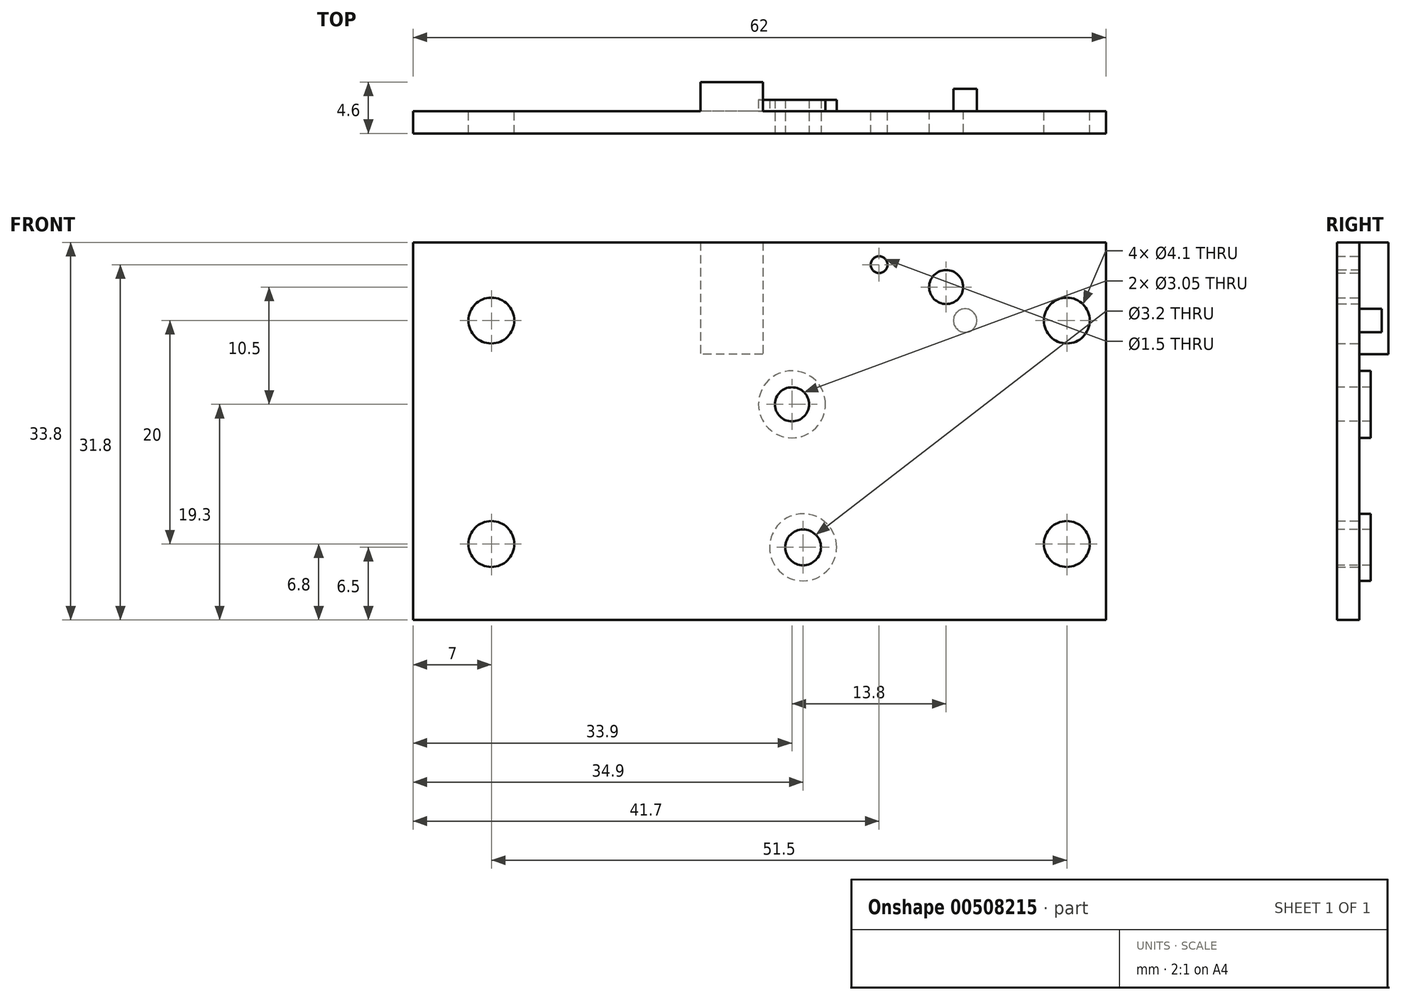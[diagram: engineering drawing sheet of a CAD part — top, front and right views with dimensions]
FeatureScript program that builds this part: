
annotation { "Feature Type Name" : "Feature", "Feature Type Description" : "" }
export const myFeature = defineFeature(function(context is Context, id is Id, definition is map)
    precondition{}
    {
        {
            var Q0;
            Q0=qCreatedBy(makeId("Front.planeOp"),FACE);
            var sketch = newSketch(context, id + "F0", { "sketchPlane" : qUnion([Q0])});
            skLineSegment(sketch, "E0.bottom", {"start": v(31, -16.9) * mm, "end": v(-31, -16.9) * mm});
            skLineSegment(sketch, "E0.top", {"start": v(31, 16.9) * mm, "end": v(-31, 16.9) * mm});
            skLineSegment(sketch, "E0.left", {"start": v(31, -16.9) * mm, "end": v(31, 16.9) * mm});
            skLineSegment(sketch, "E0.right", {"start": v(-31, -16.9) * mm, "end": v(-31, 16.9) * mm});
            skPoint(sketch, "E0.middle", {"position": v(0, 0) * mm});
            skCircle(sketch, "E1", {"center": v(16.7, 12.9) * mm, "radius": 1.52 * mm});
            skCircle(sketch, "E2", {"center": v(2.9, 2.4) * mm, "radius": 1.52 * mm});
            skCircle(sketch, "E3", {"center": v(3.9, -10.4) * mm, "radius": 1.6 * mm});
            skArc(sketch, "E4", {"start": v(6.45, 16.9) * mm, "mid": v(10.88, 3.57) * mm, "end": v(24.8, 5.46) * mm});
            skLineSegment(sketch, "E5", {"start": v(24.8, 16.9) * mm, "end": v(24.8, -16.9) * mm});
            skSolve(sketch);
        }
        {
            var Q0;
            {var subQ0=sQuery(id+"F0.wireOp",EDGE,"E0.right");Q0=makeQuery(id+"F0.imprint","IMPRINT",FACE,{"disambiguationData":[TD([[makeQuery(id+"F0.imprint","IMPRINT",EDGE,{"derivedFrom":subQ0}),-1.0]])]});}
            var Q1;
            Q1=makeQuery(id+"F0.imprint","IMPRINT",FACE,{"disambiguationData":[TD([[makeQuery(id+"F0.imprint","IMPRINT",EDGE,{"derivedFrom":sQuery(id+"F0.wireOp",EDGE,"E1")}),-1.0]])]});
            var Q2;
            {var subQ4=sQuery(id+"F0.wireOp",EDGE,"E0.left");Q2=makeQuery(id+"F0.imprint","IMPRINT",FACE,{"disambiguationData":[TD([[makeQuery(id+"F0.imprint","IMPRINT",EDGE,{"derivedFrom":subQ4}),1.0]])]});}
            extrude(context, id + "F1", {"entities" : qUnion([Q0, Q1, Q2]), "oppositeDirection" : true, "depth" : 2 * mm, "offsetDistance" : 25 * mm});
        }
        {
            var Q0;
            Q0=makeQuery(id+"F1.opExtrude","CAP_FACE",FACE,{"disambiguationData":[OSD([sQuery(id+"F0.wireOp",EDGE,"E0.bottom"),sQuery(id+"F0.wireOp",EDGE,"E0.top"),sQuery(id+"F0.wireOp",EDGE,"E0.left"),sQuery(id+"F0.wireOp",EDGE,"E0.right"),sQuery(id+"F0.wireOp",EDGE,"E1"),sQuery(id+"F0.wireOp",EDGE,"E2"),sQuery(id+"F0.wireOp",EDGE,"E3")])],"isStart":false});
            var sketch = newSketch(context, id + "F2", { "sketchPlane" : qUnion([Q0])});
            skLineSegment(sketch, "E6.bottom", {"start": v(-6, 0.4) * mm, "end": v(0, 0.4) * mm});
            skLineSegment(sketch, "E6.right", {"start": v(0, 0.4) * mm, "end": v(0, -4.1) * mm});
            skLineSegment(sketch, "E7", {"start": v(1.6, -1.8) * mm, "end": v(4.6, -1.8) * mm});
            skLineSegment(sketch, "E8", {"start": v(4.6, -1.8) * mm, "end": v(4.6, -4.8) * mm});
            skLineSegment(sketch, "E9", {"start": v(4.6, -4.8) * mm, "end": v(9.1, -4.8) * mm});
            skLineSegment(sketch, "E10", {"start": v(9.1, -4.8) * mm, "end": v(9.1, -1.8) * mm});
            skLineSegment(sketch, "E11", {"start": v(9.1, -1.8) * mm, "end": v(12.1, -1.8) * mm});
            skLineSegment(sketch, "E12", {"start": v(12.1, -1.8) * mm, "end": v(12.1, -7.3) * mm});
            skLineSegment(sketch, "E13", {"start": v(12.1, -7.3) * mm, "end": v(1.6, -7.3) * mm});
            skLineSegment(sketch, "E14", {"start": v(1.6, -7.3) * mm, "end": v(1.6, -1.8) * mm});
            skCircle(sketch, "E15.0", {"center": v(-2.9, 2.4) * mm, "radius": 1.52 * mm});
            skCircle(sketch, "E16", {"center": v(-2.9, 2.4) * mm, "radius": 3 * mm});
            skCircle(sketch, "E17.0", {"center": v(-16.7, 12.9) * mm, "radius": 1.52 * mm, "construction": true});
            skCircle(sketch, "E18", {"center": v(-10.7, 14.9) * mm, "radius": 0.75 * mm});
            skLineSegment(sketch, "E19", {"start": v(-6, 0.4) * mm, "end": v(0, -4.1) * mm});
            skCircle(sketch, "E20", {"center": v(-18.4, 9.9) * mm, "radius": 1.05 * mm});
            skLineSegment(sketch, "E21", {"start": v(4.6, -1.8) * mm, "end": v(9.1, -1.8) * mm});
            skCircle(sketch, "E22", {"center": v(-3.9, -10.4) * mm, "radius": 3 * mm});
            skCircle(sketch, "E23.0", {"center": v(-3.9, -10.4) * mm, "radius": 1.6 * mm});
            skSolve(sketch);
        }
        {
            var Q0;
            Q0=makeQuery(id+"F2.imprint","IMPRINT",FACE,{"disambiguationData":[TD([[makeQuery(id+"F2.imprint","IMPRINT",EDGE,{"derivedFrom":sQuery(id+"F2.wireOp",EDGE,"E15.0")}),1.0]])]});
            var Q1;
            {var subQ0=sQuery(id+"F2.wireOp",EDGE,"E16");var subQ1=sQuery(id+"F2.wireOp",EDGE,"E6.bottom");var subQ2=makeQuery(id+"F2.imprint","INTERSECT",VERTEX,{"disambiguationData":[OD(0.0)],"derivedFrom":[subQ1,subQ0]});Q1=makeQuery(id+"F2.imprint","IMPRINT",FACE,{"disambiguationData":[TD([[makeQuery(id+"F2.imprint","IMPRINT",EDGE,{"disambiguationData":[TD([[subQ2,-1.0]])],"derivedFrom":subQ1}),-1.0]])]});}
            var Q2;
            Q2=makeQuery(id+"F2.imprint","IMPRINT",FACE,{"disambiguationData":[TD([[makeQuery(id+"F2.imprint","IMPRINT",EDGE,{"derivedFrom":sQuery(id+"F2.wireOp",EDGE,"E22")}),1.0]])]});
            extrude(context, id + "F3", {"entities" : qUnion([Q0, Q1, Q2]), "operationType" : NewBodyOperationType.ADD, "depth" : 1 * mm, "offsetDistance" : 25 * mm});
        }
        {
            var Q0;
            Q0=makeQuery(id+"F2.imprint","IMPRINT",FACE,{"disambiguationData":[TD([[makeQuery(id+"F2.imprint","IMPRINT",EDGE,{"derivedFrom":sQuery(id+"F2.wireOp",EDGE,"E20")}),1.0]])]});
            extrude(context, id + "F4", {"entities" : qUnion([Q0]), "operationType" : NewBodyOperationType.ADD, "depth" : 2 * mm, "offsetDistance" : 25 * mm});
        }
        {
            var Q0;
            Q0=makeQuery(id+"F2.imprint","IMPRINT",FACE,{"disambiguationData":[TD([[makeQuery(id+"F2.imprint","IMPRINT",EDGE,{"derivedFrom":sQuery(id+"F2.wireOp",EDGE,"E18")}),1.0]])]});
            extrude(context, id + "F5", {"entities" : qUnion([Q0]), "operationType" : NewBodyOperationType.REMOVE, "endBound" : BoundingType.THROUGH_ALL, "oppositeDirection" : true, "depth" : 25 * mm, "offsetDistance" : 25 * mm});
        }
        {
            var Q0;
            Q0=makeQuery(id+"F2.imprint","IMPRINT",FACE,{"disambiguationData":[TD([[makeQuery(id+"F2.imprint","IMPRINT",EDGE,{"derivedFrom":sQuery(id+"F2.wireOp",EDGE,"E6.bottom")}),1.0]])]});
            var sketch = newSketch(context, id + "F6", { "sketchPlane" : qUnion([Q0])});
            skLineSegment(sketch, "E24.bottom", {"start": v(17, 16.9) * mm, "end": v(31, 16.9) * mm});
            skLineSegment(sketch, "E24.top", {"start": v(17, -16.9) * mm, "end": v(31, -16.9) * mm});
            skLineSegment(sketch, "E24.left", {"start": v(17, 16.9) * mm, "end": v(17, -16.9) * mm});
            skLineSegment(sketch, "E24.right", {"start": v(31, 16.9) * mm, "end": v(31, -16.9) * mm});
            skLineSegment(sketch, "E25.bottom", {"start": v(-31, -16.9) * mm, "end": v(-24, -16.9) * mm});
            skLineSegment(sketch, "E25.top", {"start": v(-31, 16.9) * mm, "end": v(-24, 16.9) * mm});
            skLineSegment(sketch, "E25.left", {"start": v(-31, -16.9) * mm, "end": v(-31, 16.9) * mm});
            skLineSegment(sketch, "E25.right", {"start": v(-24, -16.9) * mm, "end": v(-24, 16.9) * mm});
            skCircle(sketch, "E26", {"center": v(-27.5, 9.9) * mm, "radius": 2.05 * mm});
            skCircle(sketch, "E27", {"center": v(-27.5, -10.1) * mm, "radius": 2.05 * mm});
            skCircle(sketch, "E28", {"center": v(24, 9.9) * mm, "radius": 2.05 * mm});
            skCircle(sketch, "E29", {"center": v(24, -10.1) * mm, "radius": 2.05 * mm});
            skLineSegment(sketch, "E30", {"start": v(24, 16.9) * mm, "end": v(24, -16.9) * mm, "construction": true});
            skLineSegment(sketch, "E31", {"start": v(-27.5, 16.9) * mm, "end": v(-27.5, -16.9) * mm, "construction": true});
            skSolve(sketch);
        }
        {
            var Q0;
            Q0=makeQuery(id+"F6.imprint","IMPRINT",FACE,{"disambiguationData":[TD([[makeQuery(id+"F6.imprint","IMPRINT",EDGE,{"derivedFrom":sQuery(id+"F6.wireOp",EDGE,"E26")}),1.0]])]});
            var Q1;
            Q1=makeQuery(id+"F6.imprint","IMPRINT",FACE,{"disambiguationData":[TD([[makeQuery(id+"F6.imprint","IMPRINT",EDGE,{"derivedFrom":sQuery(id+"F6.wireOp",EDGE,"E28")}),1.0]])]});
            var Q2;
            Q2=makeQuery(id+"F6.imprint","IMPRINT",FACE,{"disambiguationData":[TD([[makeQuery(id+"F6.imprint","IMPRINT",EDGE,{"derivedFrom":sQuery(id+"F6.wireOp",EDGE,"E29")}),1.0]])]});
            var Q3;
            Q3=makeQuery(id+"F6.imprint","IMPRINT",FACE,{"disambiguationData":[TD([[makeQuery(id+"F6.imprint","IMPRINT",EDGE,{"derivedFrom":sQuery(id+"F6.wireOp",EDGE,"E27")}),1.0]])]});
            extrude(context, id + "F7", {"entities" : qUnion([Q0, Q1, Q2, Q3]), "operationType" : NewBodyOperationType.REMOVE, "endBound" : BoundingType.THROUGH_ALL, "oppositeDirection" : true, "depth" : 25 * mm, "offsetDistance" : 25 * mm});
        }
        {
            var Q0;
            {var subQ4=sQuery(id+"F2.wireOp",EDGE,"E6.right");Q0=makeQuery(id+"F2.imprint","IMPRINT",FACE,{"disambiguationData":[TD([[makeQuery(id+"F2.imprint","IMPRINT",EDGE,{"derivedFrom":subQ4}),1.0]])]});}
            var sketch = newSketch(context, id + "F8", { "sketchPlane" : qUnion([Q0])});
            skLineSegment(sketch, "E32", {"start": v(-0.3, 6.9) * mm, "end": v(5.3, 6.9) * mm});
            skLineSegment(sketch, "E33", {"start": v(5.3, 16.9) * mm, "end": v(-0.3, 16.9) * mm});
            skLineSegment(sketch, "E34", {"start": v(-0.3, 16.9) * mm, "end": v(-0.3, 6.9) * mm});
            skLineSegment(sketch, "E35", {"start": v(5.3, 16.9) * mm, "end": v(5.3, 6.9) * mm});
            skSolve(sketch);
        }
        {
            var Q0;
            Q0=makeQuery(id+"F8.imprint","IMPRINT",FACE,{"disambiguationData":[TD([[makeQuery(id+"F8.imprint","IMPRINT",EDGE,{"derivedFrom":sQuery(id+"F8.wireOp",EDGE,"E32")}),1.0]])]});
            extrude(context, id + "F9", {"entities" : qUnion([Q0]), "operationType" : NewBodyOperationType.ADD, "depth" : 2.6 * mm, "offsetDistance" : 25 * mm});
        }
    });
